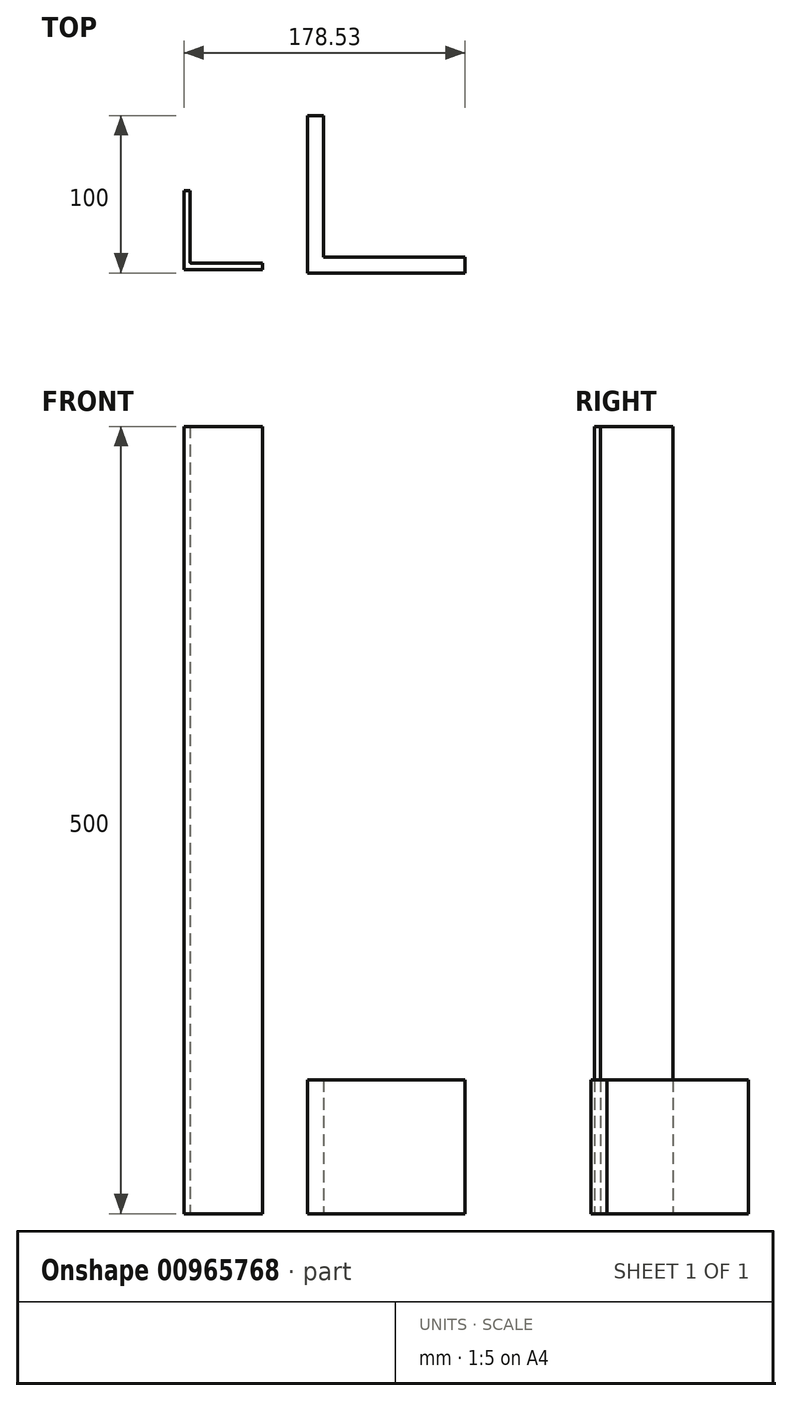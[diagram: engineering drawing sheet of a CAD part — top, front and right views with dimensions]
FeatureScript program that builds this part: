
annotation { "Feature Type Name" : "Feature", "Feature Type Description" : "" }
export const myFeature = defineFeature(function(context is Context, id is Id, definition is map)
    precondition{}
    {
        {
            var Q0;
            Q0=qCreatedBy(makeId("Top.planeOp"),FACE);
            var sketch = newSketch(context, id + "F0", { "sketchPlane" : qUnion([Q0])});
            skLineSegment(sketch, "E0", {"start": v(-25.84, 25.41) * mm, "end": v(-25.84, -24.59) * mm});
            skLineSegment(sketch, "E1", {"start": v(-25.84, -24.59) * mm, "end": v(24.16, -24.59) * mm});
            skLineSegment(sketch, "E2", {"start": v(24.16, -24.59) * mm, "end": v(24.16, -20.59) * mm});
            skLineSegment(sketch, "E3", {"start": v(24.16, -20.59) * mm, "end": v(-21.84, -20.59) * mm});
            skLineSegment(sketch, "E4", {"start": v(-21.84, -20.59) * mm, "end": v(-21.84, 25.41) * mm});
            skLineSegment(sketch, "E5", {"start": v(-21.84, 25.41) * mm, "end": v(-25.84, 25.41) * mm});
            skSolve(sketch);
        }
        {
            var Q0;
            Q0=qCreatedBy(makeId("Top.planeOp"),FACE);
            var sketch = newSketch(context, id + "F1", { "sketchPlane" : qUnion([Q0])});
            skLineSegment(sketch, "E6", {"start": v(52.69, 73.24) * mm, "end": v(52.69, -26.76) * mm});
            skLineSegment(sketch, "E7", {"start": v(52.69, -26.76) * mm, "end": v(152.69, -26.76) * mm});
            skLineSegment(sketch, "E8", {"start": v(152.69, -26.76) * mm, "end": v(152.69, -16.76) * mm});
            skLineSegment(sketch, "E9", {"start": v(152.69, -16.76) * mm, "end": v(62.69, -16.76) * mm});
            skLineSegment(sketch, "E10", {"start": v(62.69, -16.76) * mm, "end": v(62.69, 73.24) * mm});
            skLineSegment(sketch, "E11", {"start": v(62.69, 73.24) * mm, "end": v(52.69, 73.24) * mm});
            skSolve(sketch);
        }
        {
            var Q0;
            Q0 = qSketchRegion(id + "F0", true);
            extrude(context, id + "F2", {"entities" : qUnion([Q0]), "depth" : 500 * mm, "offsetDistance" : 25 * mm});
        }
        {
            var Q0;
            Q0=makeQuery(id+"F2.opExtrude","SWEPT_EDGE",EDGE,{"disambiguationData":[OSD([sQuery(id+"F0.wireOp",EDGE,"E3"),sQuery(id+"F0.wireOp",EDGE,"E4")])]});
            fillet(context, id + "F3", {"entities" : qUnion([Q0]), "radius" : .5 * mm, "tangentPropagation" : true, "allowEdgeOverflow" : false});
        }
        {
            var Q0;
            Q0 = qSketchRegion(id + "F1", true);
            extrude(context, id + "F4", {"entities" : qUnion([Q0]), "depth" : 85 * mm, "offsetDistance" : 25 * mm});
        }
    });
